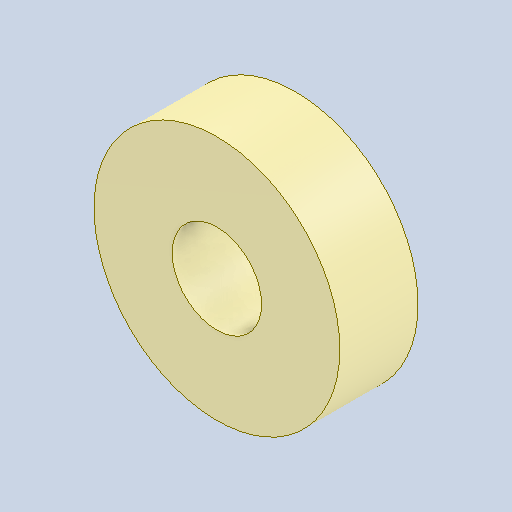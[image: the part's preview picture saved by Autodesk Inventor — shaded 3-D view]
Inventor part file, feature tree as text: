
AUTODESK INVENTOR PART (.ipt)
format: ipt  version: 2022.2 (Build 262287010, 287A)  size: 101,376 bytes
history: native  units: mm
features: extrude x1, sketch x1
ambient origin geometry x8: Origin, YZ Plane, XZ Plane, XY Plane, X Axis, Y Axis, Z Axis, Center Point
bodies: Solid1 (feature_tree)
feature tree (2):
  extrude  "Extrusion1"  Depth=7.0mm
  sketch  "Sketch1"  dims[d0=22.0mm d1=8.0mm d2=7.0mm d3=0.0mm]
